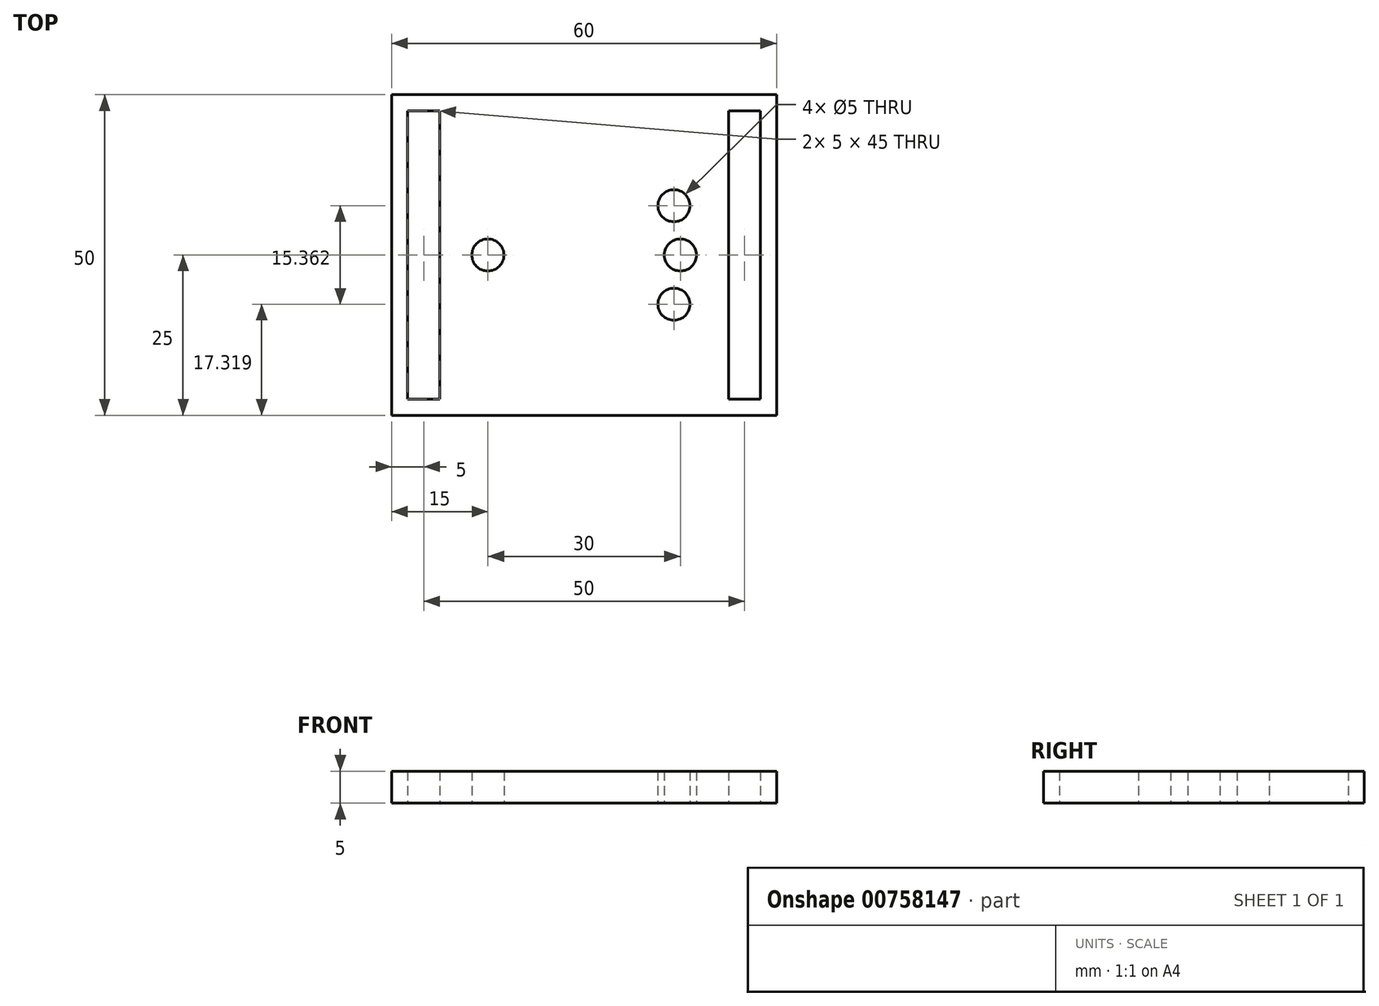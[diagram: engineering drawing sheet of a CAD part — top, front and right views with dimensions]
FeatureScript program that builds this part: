
annotation { "Feature Type Name" : "Feature", "Feature Type Description" : "" }
export const myFeature = defineFeature(function(context is Context, id is Id, definition is map)
    precondition{}
    {
        {
            var Q0;
            Q0=qCreatedBy(makeId("Top.planeOp"),FACE);
            var sketch = newSketch(context, id + "F0", { "sketchPlane" : qUnion([Q0])});
            skLineSegment(sketch, "E0.bottom", {"start": v(30, 25) * mm, "end": v(20, 25) * mm});
            skLineSegment(sketch, "E0.top", {"start": v(30, -25) * mm, "end": v(20, -25) * mm});
            skLineSegment(sketch, "E0.left", {"start": v(30, 25) * mm, "end": v(30, -25) * mm});
            skLineSegment(sketch, "E0.right", {"start": v(-30, 25) * mm, "end": v(-30, -25) * mm});
            skPoint(sketch, "E0.middle", {"position": v(0, 0) * mm});
            skLineSegment(sketch, "E1", {"start": v(-20, -25) * mm, "end": v(-20, 25) * mm});
            skLineSegment(sketch, "E2", {"start": v(20, -25) * mm, "end": v(20, 25) * mm});
            skPoint(sketch, "E3", {"position": v(-20, 25) * mm});
            skPoint(sketch, "E4", {"position": v(20, 25) * mm});
            skPoint(sketch, "E5", {"position": v(20, -25) * mm});
            skPoint(sketch, "E6", {"position": v(-20, -25) * mm});
            skLineSegment(sketch, "E7", {"start": v(-20, 25) * mm, "end": v(-30, 25) * mm});
            skLineSegment(sketch, "E8", {"start": v(20, 25) * mm, "end": v(-20, 25) * mm});
            skLineSegment(sketch, "E9", {"start": v(-20, -25) * mm, "end": v(-30, -25) * mm});
            skLineSegment(sketch, "E10", {"start": v(20, -25) * mm, "end": v(-20, -25) * mm});
            skLineSegment(sketch, "E11.0", {"start": v(-22.5, 22.5) * mm, "end": v(-27.5, 22.5) * mm});
            skLineSegment(sketch, "E11.1", {"start": v(-22.5, -22.5) * mm, "end": v(-22.5, 22.5) * mm});
            skLineSegment(sketch, "E11.2", {"start": v(-22.5, -22.5) * mm, "end": v(-27.5, -22.5) * mm});
            skLineSegment(sketch, "E11.3", {"start": v(-27.5, 22.5) * mm, "end": v(-27.5, -22.5) * mm});
            skLineSegment(sketch, "E12.0", {"start": v(27.5, 22.5) * mm, "end": v(22.5, 22.5) * mm});
            skLineSegment(sketch, "E12.1", {"start": v(27.5, 22.5) * mm, "end": v(27.5, -22.5) * mm});
            skLineSegment(sketch, "E12.2", {"start": v(27.5, -22.5) * mm, "end": v(22.5, -22.5) * mm});
            skLineSegment(sketch, "E12.3", {"start": v(22.5, -22.5) * mm, "end": v(22.5, 22.5) * mm});
            skCircle(sketch, "E13", {"center": v(15, 0) * mm, "radius": 2.5 * mm});
            skCircle(sketch, "E14", {"center": v(-15, 0) * mm, "radius": 2.5 * mm});
            skLineSegment(sketch, "E15", {"start": v(-15, 0) * mm, "end": v(-20, 0) * mm, "construction": true});
            skLineSegment(sketch, "E16", {"start": v(15, 0) * mm, "end": v(20, 0) * mm, "construction": true});
            skCircle(sketch, "E17", {"center": v(14, 7.68) * mm, "radius": 2.5 * mm});
            skCircle(sketch, "E18", {"center": v(14, -7.68) * mm, "radius": 2.5 * mm});
            skSolve(sketch);
        }
        {
            var Q0;
            Q0=makeQuery(id+"F0.imprint","IMPRINT",FACE,{"disambiguationData":[TD([[makeQuery(id+"F0.imprint","IMPRINT",EDGE,{"derivedFrom":sQuery(id+"F0.wireOp",EDGE,"E1")}),-1.0]])]});
            var Q1;
            Q1=makeQuery(id+"F0.imprint","IMPRINT",FACE,{"disambiguationData":[TD([[makeQuery(id+"F0.imprint","IMPRINT",EDGE,{"derivedFrom":sQuery(id+"F0.wireOp",EDGE,"E0.right")}),1.0]])]});
            var Q2;
            Q2=makeQuery(id+"F0.imprint","IMPRINT",FACE,{"disambiguationData":[TD([[makeQuery(id+"F0.imprint","IMPRINT",EDGE,{"derivedFrom":sQuery(id+"F0.wireOp",EDGE,"E0.bottom")}),1.0]])]});
            extrude(context, id + "F1", {"entities" : qUnion([Q0, Q1, Q2]), "depth" : 5 * mm, "offsetDistance" : 25 * mm});
        }
    });
